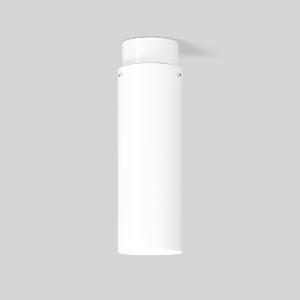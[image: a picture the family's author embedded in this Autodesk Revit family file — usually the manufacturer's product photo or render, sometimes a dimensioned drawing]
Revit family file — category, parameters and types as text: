
# Revit family: glasdownlight_931180_002_9889
name_source: partatom
category: Lighting Fixtures
units: mm (PartAtom-declared; Revit-internal decimal feet)

## family parameters
Cut with Voids When Loaded = No
Host = Face
Light Source = No
Part Type = Normal
Room Calculation Point = No
Round Connector Dimension = Use Diameter
Shared = No

## types (1)
- GLASDOWNLIGHT (1 x LED Modul 830, 2600 lm, 3000)
    Apparent Load = 20 VA
    CIE Flux Codes = 22 47 73 55 100
    Color Rendering = 80
    Color Temperature = 3000
    Default Elevation = 1800 mm
    Description = Series: GLASDOWNLIGHT
Decorative round surface-mounted luminaire. Base: aluminium, powder-coated. Mouth blown 3-layer opal glass (Triplex glass) with satin finish. Glass fastening: retaining screws. Triplex glass produces particularly homogeneous, soft and glare free lighting. 
Colour: white
Diameter: 150 mm
Height: 470 mm
Lamp: LED
Socket: without socket
Colour temperature: 3000K
Colour rendering index (CRI): 80
System power: 20 W
Rated luminous flux: 2600 lm
Luminous efficiency: 130 lm/W
Control gear: Regulated power supply
Protection class: I
Type of protection: IP 20
    Height = 470 mm
    Lamp = 1 x LED Modul 830
    Lamp Light Flux = 2600 lm
    Lamp count = 1
    Length = 150 mm
    Lifetime = 50000 h
    Luminous efficacy = 130 lm/W
    Manufacturer = RZB
    ModVariant = No
    Model = 931180.002
    Mounting Place = Ceiling
    Mounting Type = Surface mounted
    Number of Poles = 1
    OnlyDefault = Yes
    Power Factor = 1
    Product Name = GLASDOWNLIGHT
    Product group = Surface mounted ceiling luminaires
    ProductGroupID = 303
    Protection Class = Protection class I
    Protection Degree = IP 20
    RLX_Detail_Level = 1
    RLX_Emergency_Light_Flux = 0 lm
    RLX_Emergency_Type = 0
    RLX_Emergency_Type_DB = No
    RlxData = <blob elided: 15429 chars, md5=139f4049>
    Socket = socket
    Standby Power = 0 W
    System Light Flux = 2600 lm
    System Power = 20 W
    Type Comments = Product without accessories
    Type Image = 931180.002.jpg
    URL = http://relux.com
    VarID = ---
    Voltage = 230 V
    Voltage Range = 220-240 V
    Weight = 0.00 kg
    Width = 0 mm  [stored 0 ft]

note: [stored X ft] marks values corroborated as IEEE doubles in the binary element streams (Revit-internal decimal feet)

## geometry (parser evidence)
native form markers: Sweep x15
no freeform markers — native parametric forms only
